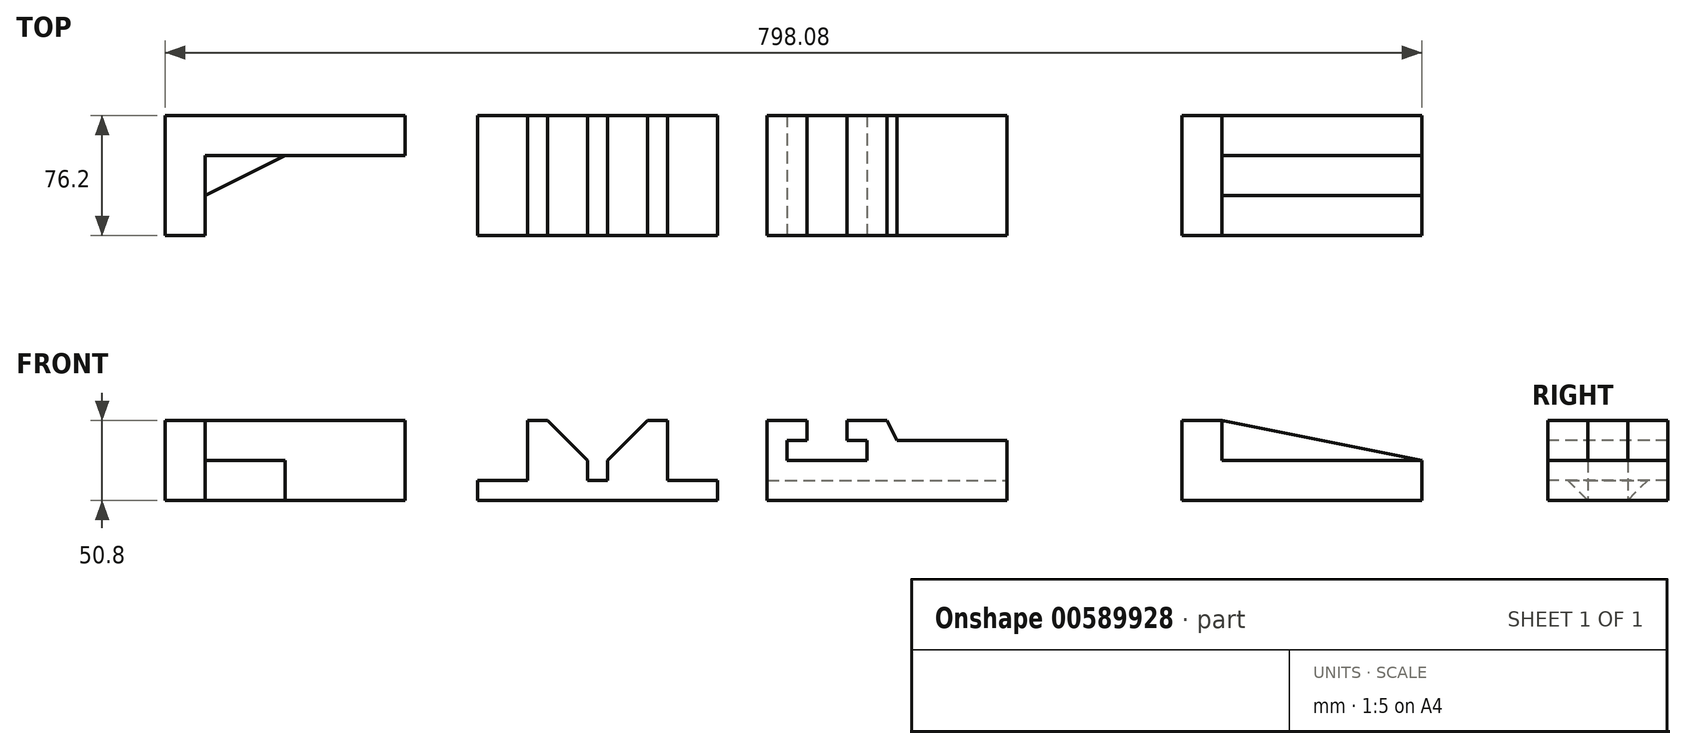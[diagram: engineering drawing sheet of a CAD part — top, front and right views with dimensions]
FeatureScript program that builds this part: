
annotation { "Feature Type Name" : "Feature", "Feature Type Description" : "" }
export const myFeature = defineFeature(function(context is Context, id is Id, definition is map)
    precondition{}
    {
        {
            var Q0;
            Q0=qCreatedBy(makeId("Top.planeOp"),FACE);
            var sketch = newSketch(context, id + "F0", { "sketchPlane" : qUnion([Q0])});
            skLineSegment(sketch, "E0", {"start": v(161.3, 0) * mm, "end": v(161.3, 76.2) * mm});
            skLineSegment(sketch, "E1", {"start": v(161.3, 76.2) * mm, "end": v(313.7, 76.2) * mm});
            skLineSegment(sketch, "E2", {"start": v(313.7, 76.2) * mm, "end": v(313.7, 50.8) * mm});
            skLineSegment(sketch, "E3", {"start": v(313.7, 50.8) * mm, "end": v(237.5, 50.8) * mm});
            skLineSegment(sketch, "E4", {"start": v(161.3, 0) * mm, "end": v(186.7, 0) * mm});
            skLineSegment(sketch, "E5", {"start": v(186.7, 0) * mm, "end": v(186.7, 25.4) * mm});
            skLineSegment(sketch, "E6", {"start": v(186.7, 25.4) * mm, "end": v(237.5, 50.8) * mm});
            skSolve(sketch);
        }
        {
            var Q0;
            Q0=makeQuery(id+"F0.imprint","IMPRINT",FACE,{"disambiguationData":[TD([[makeQuery(id+"F0.imprint","IMPRINT",EDGE,{"derivedFrom":sQuery(id+"F0.wireOp",EDGE,"E0")}),-1.0]])]});
            extrude(context, id + "F1", {"entities" : qUnion([Q0]), "depth" : 50.8 * mm, "offsetDistance" : 25.4 * mm});
        }
        {
            var Q0;
            Q0=makeQuery(id+"F1.opExtrude","CAP_FACE",FACE,{"disambiguationData":[OSD([sQuery(id+"F0.wireOp",EDGE,"E0"),sQuery(id+"F0.wireOp",EDGE,"E1"),sQuery(id+"F0.wireOp",EDGE,"E2"),sQuery(id+"F0.wireOp",EDGE,"E3"),sQuery(id+"F0.wireOp",EDGE,"E4"),sQuery(id+"F0.wireOp",EDGE,"E5"),sQuery(id+"F0.wireOp",EDGE,"E6")])],"isStart":false});
            var sketch = newSketch(context, id + "F2", { "sketchPlane" : qUnion([Q0])});
            skLineSegment(sketch, "E7", {"start": v(186.7, 25.4) * mm, "end": v(186.7, 50.8) * mm});
            skLineSegment(sketch, "E8", {"start": v(186.7, 50.8) * mm, "end": v(237.5, 50.8) * mm});
            skSolve(sketch);
        }
        {
            var Q0;
            Q0=makeQuery(id+"F2.imprint","IMPRINT",FACE,{"disambiguationData":[TD([[makeQuery(id+"F2.imprint","IMPRINT",EDGE,{"derivedFrom":sQuery(id+"F2.wireOp",EDGE,"E7")}),-1.0]])]});
            extrude(context, id + "F3", {"entities" : qUnion([Q0]), "operationType" : NewBodyOperationType.REMOVE, "oppositeDirection" : true, "depth" : 25.4 * mm, "offsetDistance" : 25.4 * mm});
        }
        {
            var Q0;
            Q0=qCreatedBy(makeId("Front.planeOp"),FACE);
            var sketch = newSketch(context, id + "F4", { "sketchPlane" : qUnion([Q0])});
            skLineSegment(sketch, "E9", {"start": v(359.64, 0) * mm, "end": v(359.64, 12.7) * mm});
            skLineSegment(sketch, "E10", {"start": v(359.64, 12.7) * mm, "end": v(391.4, 12.7) * mm});
            skLineSegment(sketch, "E11", {"start": v(391.4, 12.7) * mm, "end": v(391.4, 50.8) * mm});
            skLineSegment(sketch, "E12", {"start": v(391.4, 50.8) * mm, "end": v(404.1, 50.8) * mm});
            skLineSegment(sketch, "E13", {"start": v(359.64, 0) * mm, "end": v(512.04, 0) * mm});
            skLineSegment(sketch, "E14", {"start": v(512.04, 0) * mm, "end": v(512.04, 12.7) * mm});
            skLineSegment(sketch, "E15", {"start": v(512.04, 12.7) * mm, "end": v(480.3, 12.7) * mm});
            skLineSegment(sketch, "E16", {"start": v(480.3, 12.7) * mm, "end": v(480.3, 50.8) * mm});
            skLineSegment(sketch, "E17", {"start": v(480.3, 50.8) * mm, "end": v(467.6, 50.8) * mm});
            skLineSegment(sketch, "E18", {"start": v(429.5, 12.7) * mm, "end": v(429.5, 25.4) * mm});
            skLineSegment(sketch, "E19", {"start": v(429.5, 12.7) * mm, "end": v(442.2, 12.7) * mm});
            skLineSegment(sketch, "E20", {"start": v(442.2, 12.7) * mm, "end": v(442.2, 25.4) * mm});
            skLineSegment(sketch, "E21", {"start": v(404.1, 50.8) * mm, "end": v(429.5, 25.4) * mm});
            skLineSegment(sketch, "E22", {"start": v(442.2, 25.4) * mm, "end": v(467.6, 50.8) * mm});
            skSolve(sketch);
        }
        {
            var Q0;
            Q0=makeQuery(id+"F4.imprint","IMPRINT",FACE,{"disambiguationData":[TD([[makeQuery(id+"F4.imprint","IMPRINT",EDGE,{"derivedFrom":sQuery(id+"F4.wireOp",EDGE,"E9")}),-1.0]])]});
            extrude(context, id + "F5", {"entities" : qUnion([Q0]), "oppositeDirection" : true, "depth" : 76.2 * mm, "offsetDistance" : 25.4 * mm});
        }
        {
            var Q0;
            Q0=qCreatedBy(makeId("Front.planeOp"),FACE);
            var sketch = newSketch(context, id + "F6", { "sketchPlane" : qUnion([Q0])});
            skLineSegment(sketch, "E23", {"start": v(543.54, 0) * mm, "end": v(543.54, 50.8) * mm});
            skLineSegment(sketch, "E24", {"start": v(543.54, 50.8) * mm, "end": v(568.94, 50.8) * mm});
            skLineSegment(sketch, "E25", {"start": v(568.94, 50.8) * mm, "end": v(568.94, 38.1) * mm});
            skLineSegment(sketch, "E26", {"start": v(568.94, 38.1) * mm, "end": v(556.24, 38.1) * mm});
            skLineSegment(sketch, "E27", {"start": v(556.24, 38.1) * mm, "end": v(556.24, 25.4) * mm});
            skLineSegment(sketch, "E28", {"start": v(556.24, 25.4) * mm, "end": v(607.04, 25.4) * mm});
            skLineSegment(sketch, "E29", {"start": v(607.04, 25.4) * mm, "end": v(607.04, 38.1) * mm});
            skLineSegment(sketch, "E30", {"start": v(607.04, 38.1) * mm, "end": v(594.34, 38.1) * mm});
            skLineSegment(sketch, "E31", {"start": v(594.34, 38.1) * mm, "end": v(594.34, 50.8) * mm});
            skLineSegment(sketch, "E32", {"start": v(594.34, 50.8) * mm, "end": v(619.74, 50.8) * mm});
            skLineSegment(sketch, "E33", {"start": v(543.54, 0) * mm, "end": v(695.94, 0) * mm});
            skLineSegment(sketch, "E34", {"start": v(695.94, 0) * mm, "end": v(695.94, 38.1) * mm});
            skLineSegment(sketch, "E35", {"start": v(695.94, 38.1) * mm, "end": v(626.1, 38.1) * mm});
            skLineSegment(sketch, "E36", {"start": v(626.1, 38.1) * mm, "end": v(619.74, 50.8) * mm});
            skSolve(sketch);
        }
        {
            var Q0;
            Q0=makeQuery(id+"F6.imprint","IMPRINT",FACE,{"disambiguationData":[TD([[makeQuery(id+"F6.imprint","IMPRINT",EDGE,{"derivedFrom":sQuery(id+"F6.wireOp",EDGE,"E23")}),-1.0]])]});
            extrude(context, id + "F7", {"entities" : qUnion([Q0]), "oppositeDirection" : true, "depth" : 76.2 * mm, "offsetDistance" : 25.4 * mm});
        }
        {
            var Q0;
            Q0=makeQuery(id+"F7.opExtrude","SWEPT_FACE",FACE,{"disambiguationData":[OSD([sQuery(id+"F6.wireOp",EDGE,"E34")])]});
            var sketch = newSketch(context, id + "F8", { "sketchPlane" : qUnion([Q0])});
            skLineSegment(sketch, "E37", {"start": v(12.7, 12.7) * mm, "end": v(63.5, 12.7) * mm});
            skLineSegment(sketch, "E38", {"start": v(25.4, 0) * mm, "end": v(12.7, 12.7) * mm});
            skLineSegment(sketch, "E39", {"start": v(50.8, 0) * mm, "end": v(63.5, 12.7) * mm});
            skSolve(sketch);
        }
        {
            var Q0;
            Q0=makeQuery(id+"F8.imprint","IMPRINT",FACE,{"disambiguationData":[TD([[makeQuery(id+"F8.imprint","IMPRINT",EDGE,{"derivedFrom":sQuery(id+"F8.wireOp",EDGE,"E37")}),-1.0]])]});
            extrude(context, id + "F9", {"entities" : qUnion([Q0]), "operationType" : NewBodyOperationType.REMOVE, "oppositeDirection" : true, "depth" : 167.39 * mm, "offsetDistance" : 25.4 * mm});
        }
        {
            var Q0;
            Q0=qCreatedBy(makeId("Top.planeOp"),FACE);
            var sketch = newSketch(context, id + "F10", { "sketchPlane" : qUnion([Q0])});
            skLineSegment(sketch, "E40", {"start": v(806.98, 0) * mm, "end": v(806.98, 76.2) * mm});
            skLineSegment(sketch, "E41", {"start": v(806.98, 76.2) * mm, "end": v(959.38, 76.2) * mm});
            skLineSegment(sketch, "E42", {"start": v(959.38, 76.2) * mm, "end": v(959.38, 0) * mm});
            skLineSegment(sketch, "E43", {"start": v(959.38, 0) * mm, "end": v(806.98, 0) * mm});
            skSolve(sketch);
        }
        {
            var Q0;
            Q0=makeQuery(id+"F10.imprint","IMPRINT",FACE,{"disambiguationData":[TD([[makeQuery(id+"F10.imprint","IMPRINT",EDGE,{"derivedFrom":sQuery(id+"F10.wireOp",EDGE,"E40")}),-1.0]])]});
            extrude(context, id + "F11", {"entities" : qUnion([Q0]), "depth" : 50.8 * mm, "offsetDistance" : 25.4 * mm});
        }
        {
            var Q0;
            Q0=makeQuery(id+"F11.opExtrude","SWEPT_FACE",FACE,{"disambiguationData":[OSD([sQuery(id+"F10.wireOp",EDGE,"E43")])]});
            var sketch = newSketch(context, id + "F12", { "sketchPlane" : qUnion([Q0])});
            skLineSegment(sketch, "E44.bottom", {"start": v(959.38, 50.8) * mm, "end": v(832.38, 50.8) * mm});
            skLineSegment(sketch, "E44.top", {"start": v(959.38, 25.4) * mm, "end": v(832.38, 25.4) * mm});
            skLineSegment(sketch, "E44.left", {"start": v(959.38, 50.8) * mm, "end": v(959.38, 25.4) * mm});
            skLineSegment(sketch, "E44.right", {"start": v(832.38, 50.8) * mm, "end": v(832.38, 25.4) * mm});
            skSolve(sketch);
        }
        {
            var Q0;
            Q0=makeQuery(id+"F12.imprint","IMPRINT",FACE,{"disambiguationData":[TD([[makeQuery(id+"F12.imprint","IMPRINT",EDGE,{"derivedFrom":sQuery(id+"F12.wireOp",EDGE,"E44.bottom")}),1.0]])]});
            extrude(context, id + "F13", {"entities" : qUnion([Q0]), "operationType" : NewBodyOperationType.REMOVE, "oppositeDirection" : true, "depth" : 25.4 * mm, "offsetDistance" : 25.4 * mm});
        }
        {
            var Q0;
            Q0=makeQuery(id+"F11.opExtrude","SWEPT_FACE",FACE,{"disambiguationData":[OSD([sQuery(id+"F10.wireOp",EDGE,"E41")])]});
            var sketch = newSketch(context, id + "F14", { "sketchPlane" : qUnion([Q0])});
            skLineSegment(sketch, "E45.bottom", {"start": v(-959.38, 50.8) * mm, "end": v(-832.38, 50.8) * mm});
            skLineSegment(sketch, "E45.top", {"start": v(-959.38, 25.4) * mm, "end": v(-832.38, 25.4) * mm});
            skLineSegment(sketch, "E45.left", {"start": v(-959.38, 50.8) * mm, "end": v(-959.38, 25.4) * mm});
            skLineSegment(sketch, "E45.right", {"start": v(-832.38, 50.8) * mm, "end": v(-832.38, 25.4) * mm});
            skSolve(sketch);
        }
        {
            var Q0;
            Q0=makeQuery(id+"F14.imprint","IMPRINT",FACE,{"disambiguationData":[TD([[makeQuery(id+"F14.imprint","IMPRINT",EDGE,{"derivedFrom":sQuery(id+"F14.wireOp",EDGE,"E45.bottom")}),1.0]])]});
            extrude(context, id + "F15", {"entities" : qUnion([Q0]), "operationType" : NewBodyOperationType.REMOVE, "oppositeDirection" : true, "depth" : 25.4 * mm, "offsetDistance" : 25.4 * mm});
        }
        {
            var Q0;
            Q0=makeQuery(id+"F13.boolean.opBoolean","COPY",FACE,{"derivedFrom":makeQuery(id+"F13.opExtrude","CAP_FACE",FACE,{"disambiguationData":[OSD([sQuery(id+"F12.wireOp",EDGE,"E44.bottom"),sQuery(id+"F12.wireOp",EDGE,"E44.top"),sQuery(id+"F12.wireOp",EDGE,"E44.left"),sQuery(id+"F12.wireOp",EDGE,"E44.right")])],"isStart":false})});
            var sketch = newSketch(context, id + "F16", { "sketchPlane" : qUnion([Q0])});
            skLineSegment(sketch, "E46", {"start": v(832.38, 50.8) * mm, "end": v(959.38, 25.4) * mm});
            skSolve(sketch);
        }
        {
            var Q0;
            Q0=makeQuery(id+"F16.imprint","IMPRINT",FACE,{"disambiguationData":[TD([[makeQuery(id+"F16.imprint","IMPRINT",EDGE,{"derivedFrom":sQuery(id+"F16.wireOp",EDGE,"E46")}),1.0]])]});
            extrude(context, id + "F17", {"entities" : qUnion([Q0]), "operationType" : NewBodyOperationType.REMOVE, "oppositeDirection" : true, "depth" : 25.4 * mm, "offsetDistance" : 25.4 * mm});
        }
    });
